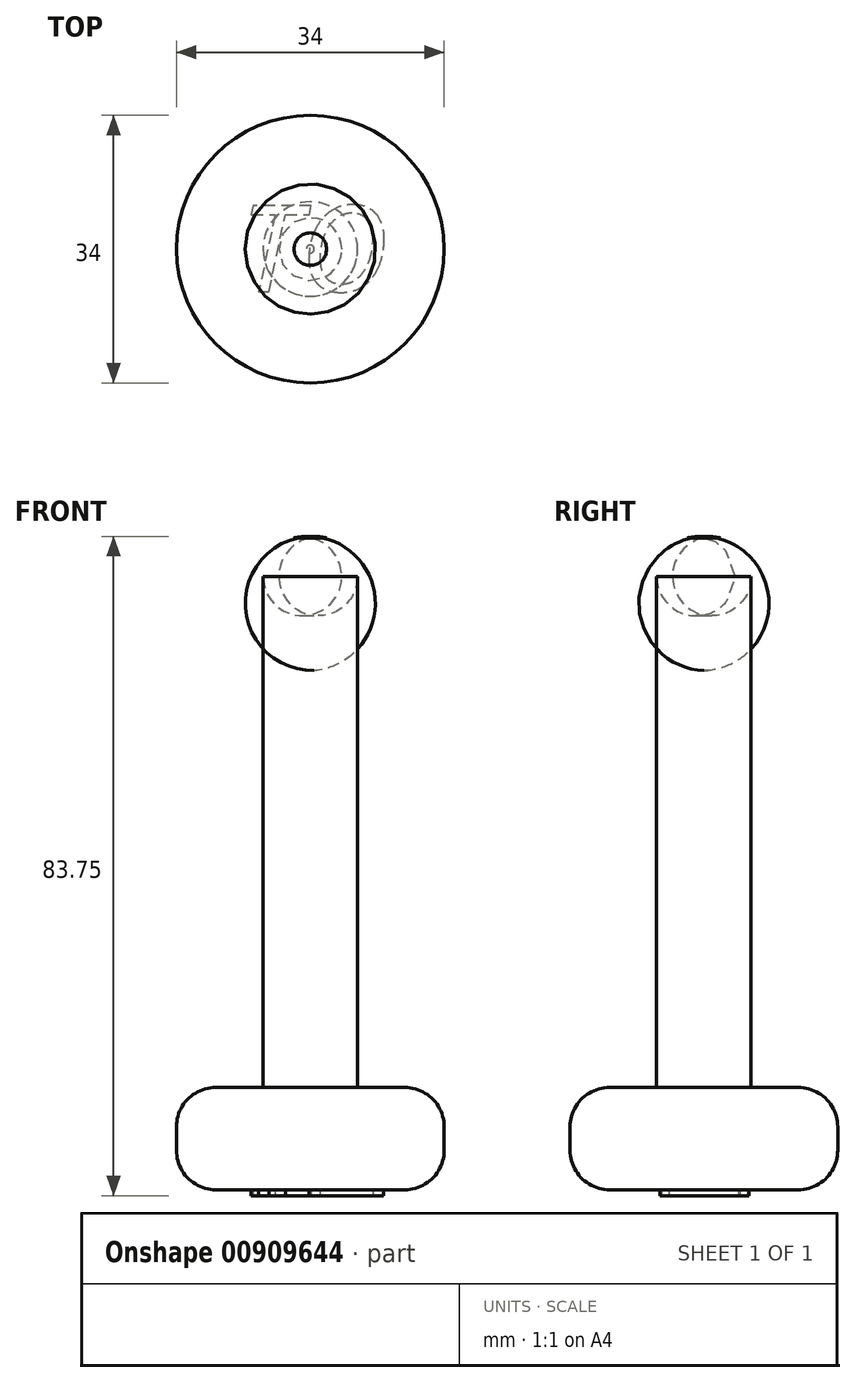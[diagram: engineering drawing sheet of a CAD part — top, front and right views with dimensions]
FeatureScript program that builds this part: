
annotation { "Feature Type Name" : "Feature", "Feature Type Description" : "" }
export const myFeature = defineFeature(function(context is Context, id is Id, definition is map)
    precondition{}
    {
        {
            var Q0;
            Q0=qCreatedBy(makeId("Front.planeOp"),FACE);
            var sketch = newSketch(context, id + "F0", { "sketchPlane" : qUnion([Q0])});
            skLineSegment(sketch, "E0", {"start": v(0, 83) * mm, "end": v(0, 0) * mm});
            skLineSegment(sketch, "E1", {"start": v(0, 0) * mm, "end": v(17, 0) * mm});
            skLineSegment(sketch, "E2", {"start": v(17, 0) * mm, "end": v(17, 13) * mm});
            skLineSegment(sketch, "E3", {"start": v(17, 13) * mm, "end": v(6, 13) * mm});
            skLineSegment(sketch, "E4", {"start": v(6, 13) * mm, "end": v(6, 80.77) * mm});
            skArc(sketch, "E5", {"start": v(6, 80.77) * mm, "mid": v(3.22, 82.47) * mm, "end": v(0, 83) * mm});
            skSolve(sketch);
        }
        {
            var Q0;
            Q0=makeQuery(id+"F0.imprint","IMPRINT",FACE,{"disambiguationData":[TD([[makeQuery(id+"F0.imprint","IMPRINT",EDGE,{"derivedFrom":sQuery(id+"F0.wireOp",EDGE,"E0")}),1.0]])]});
            var Q1;
            Q1=sQuery(id+"F0.wireOp",EDGE,"E0");
            revolve(context, id + "F1", {"surfaceOperationType" : NewSurfaceOperationType.NEW, "entities" : qUnion([Q0]), "axis" : qUnion([Q1]), "revolveType" : RevolveType.FULL});
        }
        {
            var Q0;
            Q0=makeQuery(id+"F1.opRevolve","SWEPT_EDGE",EDGE,{"disambiguationData":[OSD([sQuery(id+"F0.wireOp",EDGE,"E2"),sQuery(id+"F0.wireOp",EDGE,"E3")])]});
            fillet(context, id + "F2", {"entities" : qUnion([Q0]), "radius" : 5 * mm, "tangentPropagation" : true, "allowEdgeOverflow" : false});
        }
        {
            var Q0;
            Q0=makeQuery(id+"F1.opRevolve","SWEPT_EDGE",EDGE,{"disambiguationData":[OSD([sQuery(id+"F0.wireOp",EDGE,"E1"),sQuery(id+"F0.wireOp",EDGE,"E2")])]});
            fillet(context, id + "F3", {"entities" : qUnion([Q0]), "radius" : 5 * mm, "tangentPropagation" : true, "allowEdgeOverflow" : false});
        }
        {
            var Q0;
            Q0=qCreatedBy(makeId("Top.planeOp"),FACE);
            var sketch = newSketch(context, id + "F4", { "sketchPlane" : qUnion([Q0])});
            skText(sketch, "E6", { "text": "TO", "fontName": "OpenSans-Italic.ttf"});
            const initialGuessF4  = {"E6": [-0.0089, -0.00542, 1, 0, 0.01105]};
            skSetInitialGuess(sketch, initialGuessF4);
            skSolve(sketch);
        }
        {
            var Q0;
            Q0 = qSketchRegion(id + "F4", true);
            extrude(context, id + "F5", {"entities" : qUnion([Q0]), "operationType" : NewBodyOperationType.ADD, "endBound" : BoundingType.SYMMETRIC, "depth" : 1.5 * mm, "offsetDistance" : 25 * mm});
        }
        {
            var Q0;
            Q0=makeQuery(id+"F1.opRevolve","SWEPT_EDGE",EDGE,{"disambiguationData":[OSD([sQuery(id+"F0.wireOp",EDGE,"E4"),sQuery(id+"F0.wireOp",EDGE,"E5")])]});
            fillet(context, id + "F6", {"entities" : qUnion([Q0]), "radius" : 5 * mm, "tangentPropagation" : true, "allowEdgeOverflow" : false});
        }
    });
